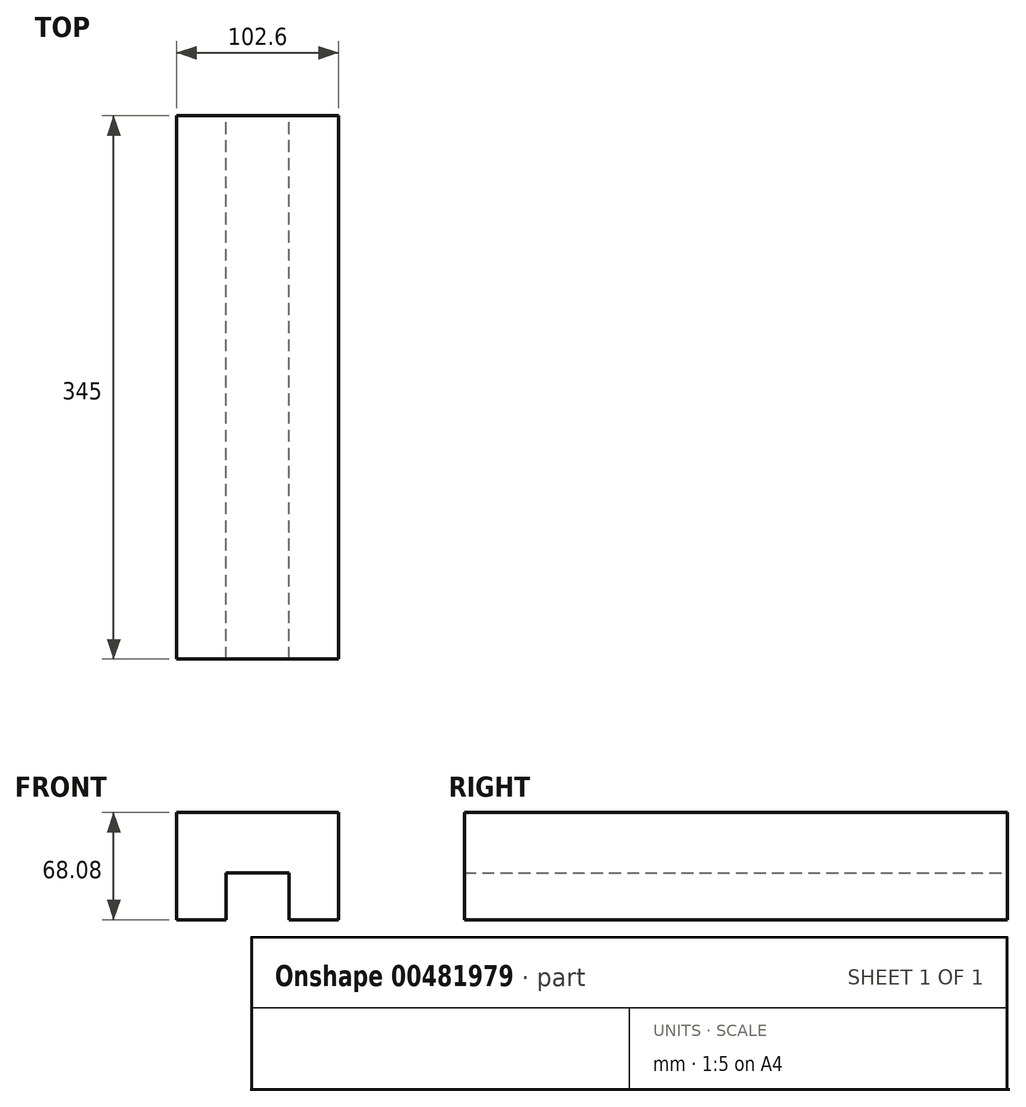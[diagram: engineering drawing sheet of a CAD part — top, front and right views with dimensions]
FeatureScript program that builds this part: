
annotation { "Feature Type Name" : "Feature", "Feature Type Description" : "" }
export const myFeature = defineFeature(function(context is Context, id is Id, definition is map)
    precondition{}
    {
        {
            var Q0;
            Q0=qCreatedBy(makeId("Front.planeOp"),FACE);
            var sketch = newSketch(context, id + "F0", { "sketchPlane" : qUnion([Q0])});
            skLineSegment(sketch, "E0.bottom", {"start": v(-53.58, 15.3) * mm, "end": v(49.02, 15.3) * mm});
            skLineSegment(sketch, "E0.top", {"start": v(-53.58, -22.96) * mm, "end": v(49.02, -22.96) * mm});
            skLineSegment(sketch, "E0.left", {"start": v(-53.58, 15.3) * mm, "end": v(-53.58, -22.96) * mm});
            skLineSegment(sketch, "E0.right", {"start": v(49.02, 15.3) * mm, "end": v(49.02, -22.96) * mm});
            skLineSegment(sketch, "E1.bottom", {"start": v(-53.58, 15.3) * mm, "end": v(-22.28, 15.3) * mm});
            skLineSegment(sketch, "E1.top", {"start": v(-53.58, -52.77) * mm, "end": v(-22.28, -52.77) * mm});
            skLineSegment(sketch, "E1.left", {"start": v(-53.58, 15.3) * mm, "end": v(-53.58, -52.77) * mm});
            skLineSegment(sketch, "E1.right", {"start": v(-22.28, 15.3) * mm, "end": v(-22.28, -52.77) * mm});
            skLineSegment(sketch, "E2.bottom", {"start": v(49.02, 15.3) * mm, "end": v(17.72, 15.3) * mm});
            skLineSegment(sketch, "E2.top", {"start": v(49.02, -52.77) * mm, "end": v(17.72, -52.77) * mm});
            skLineSegment(sketch, "E2.left", {"start": v(49.02, 15.3) * mm, "end": v(49.02, -52.77) * mm});
            skLineSegment(sketch, "E2.right", {"start": v(17.72, 15.3) * mm, "end": v(17.72, -52.77) * mm});
            skSolve(sketch);
        }
        {
            var Q0;
            {var subQ5=sQuery(id+"F0.wireOp",EDGE,"E1.top");Q0=makeQuery(id+"F0.imprint","IMPRINT",FACE,{"disambiguationData":[TD([[makeQuery(id+"F0.imprint","IMPRINT",EDGE,{"derivedFrom":subQ5}),1.0]])]});}
            var Q1;
            {var subQ5=sQuery(id+"F0.wireOp",EDGE,"E1.bottom");Q1=makeQuery(id+"F0.imprint","IMPRINT",FACE,{"disambiguationData":[TD([[makeQuery(id+"F0.imprint","IMPRINT",EDGE,{"derivedFrom":subQ5}),-1.0]])]});}
            var Q2;
            {var subQ0=sQuery(id+"F0.wireOp",EDGE,"E0.bottom");Q2=makeQuery(id+"F0.imprint","IMPRINT",FACE,{"disambiguationData":[TD([[makeQuery(id+"F0.imprint","IMPRINT",EDGE,{"derivedFrom":subQ0}),-1.0]])]});}
            var Q3;
            {var subQ5=sQuery(id+"F0.wireOp",EDGE,"E2.bottom");Q3=makeQuery(id+"F0.imprint","IMPRINT",FACE,{"disambiguationData":[TD([[makeQuery(id+"F0.imprint","IMPRINT",EDGE,{"derivedFrom":subQ5}),1.0]])]});}
            var Q4;
            {var subQ5=sQuery(id+"F0.wireOp",EDGE,"E2.top");Q4=makeQuery(id+"F0.imprint","IMPRINT",FACE,{"disambiguationData":[TD([[makeQuery(id+"F0.imprint","IMPRINT",EDGE,{"derivedFrom":subQ5}),-1.0]])]});}
            extrude(context, id + "F1", {"entities" : qUnion([Q0, Q1, Q2, Q3, Q4]), "depth" : 345 * mm});
        }
    });
